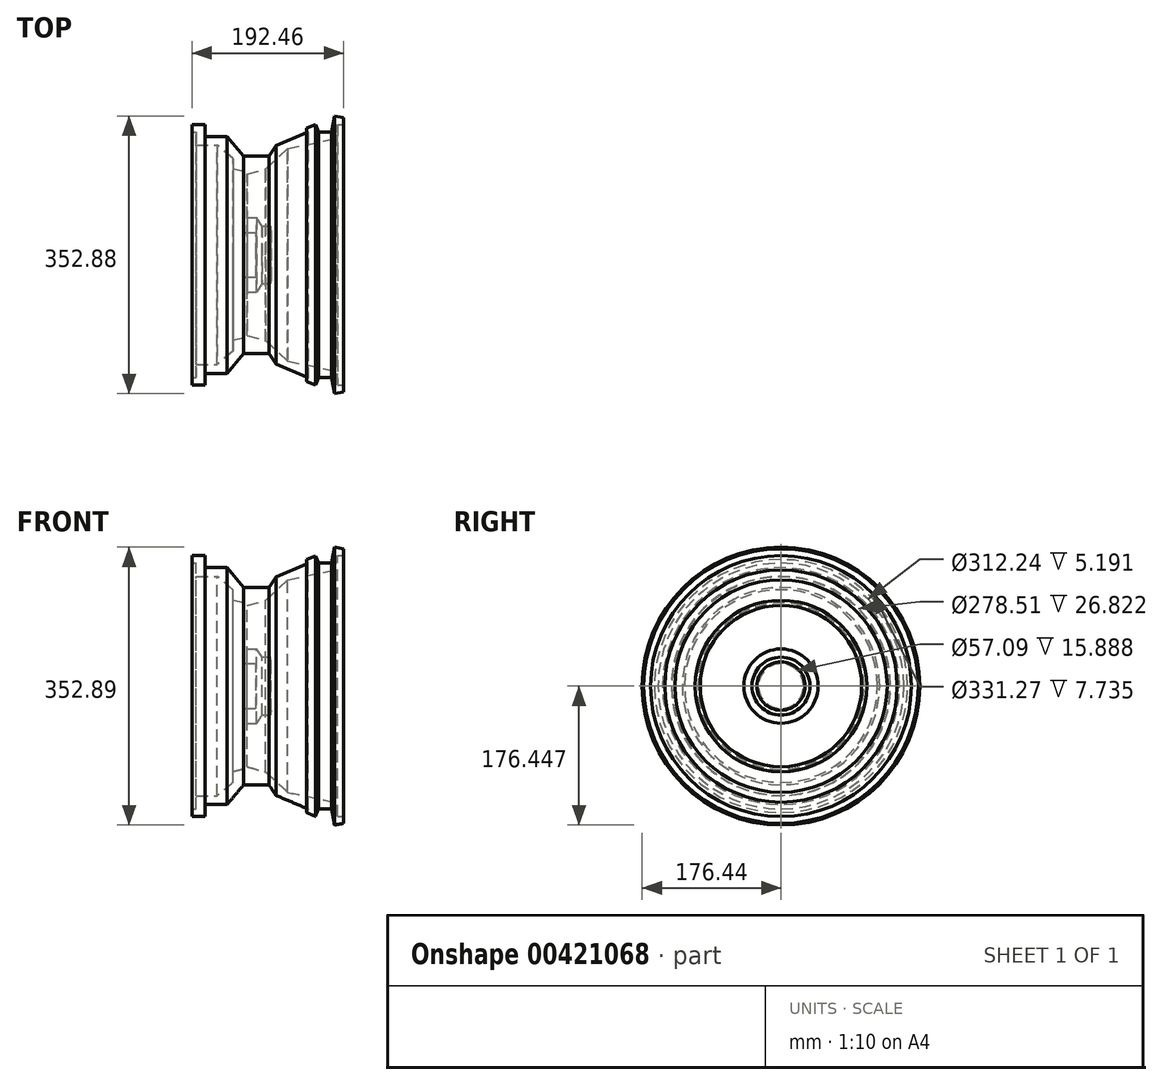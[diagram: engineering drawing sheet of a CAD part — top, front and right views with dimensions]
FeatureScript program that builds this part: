
annotation { "Feature Type Name" : "Feature", "Feature Type Description" : "" }
export const myFeature = defineFeature(function(context is Context, id is Id, definition is map)
    precondition{}
    {
        {
            var Q0;
            Q0=qCreatedBy(makeId("Front.planeOp"),FACE);
            var sketch = newSketch(context, id + "F0", { "sketchPlane" : qUnion([Q0])});
            skLineSegment(sketch, "E0", {"start": v(-30.6, 50.28) * mm, "end": v(-5.54, 50.28) * mm});
            skLineSegment(sketch, "E1", {"start": v(-5.54, 50.28) * mm, "end": v(-5.54, 46.5) * mm});
            skLineSegment(sketch, "E2", {"start": v(-5.54, 46.5) * mm, "end": v(9.91, 49.4) * mm});
            skLineSegment(sketch, "E3", {"start": v(9.91, 49.4) * mm, "end": v(36.73, 45.32) * mm});
            skLineSegment(sketch, "E4", {"start": v(36.73, 45.32) * mm, "end": v(36.73, 29.88) * mm});
            skLineSegment(sketch, "E5", {"start": v(36.73, 29.88) * mm, "end": v(22.15, 11.22) * mm});
            skLineSegment(sketch, "E6", {"start": v(22.15, 11.22) * mm, "end": v(18.07, -13.55) * mm});
            skLineSegment(sketch, "E7", {"start": v(18.07, -13.55) * mm, "end": v(31.19, -23.46) * mm});
            skLineSegment(sketch, "E8", {"start": v(31.19, -23.46) * mm, "end": v(11.37, -29.88) * mm});
            skLineSegment(sketch, "E9", {"start": v(11.37, -29.88) * mm, "end": v(2.33, -12.1) * mm});
            skLineSegment(sketch, "E10", {"start": v(2.33, -12.1) * mm, "end": v(-20.99, -20.26) * mm});
            skLineSegment(sketch, "E11", {"start": v(-20.99, -20.26) * mm, "end": v(-29.44, -6.85) * mm});
            skLineSegment(sketch, "E12", {"start": v(-29.44, -6.85) * mm, "end": v(-29.44, 11.51) * mm});
            skLineSegment(sketch, "E13", {"start": v(-29.44, 11.51) * mm, "end": v(-37.6, 25.21) * mm});
            skLineSegment(sketch, "E14", {"start": v(-37.6, 25.21) * mm, "end": v(-37.6, 39.79) * mm});
            skLineSegment(sketch, "E15", {"start": v(-37.6, 39.79) * mm, "end": v(-62.38, 46.5) * mm});
            skLineSegment(sketch, "E16", {"start": v(-62.38, 46.5) * mm, "end": v(-62.38, 55.23) * mm});
            skLineSegment(sketch, "E17", {"start": v(-62.38, 55.23) * mm, "end": v(-67.33, 55.23) * mm});
            skLineSegment(sketch, "E18", {"start": v(-67.33, 55.23) * mm, "end": v(-67.33, 61.36) * mm});
            skLineSegment(sketch, "E19", {"start": v(-67.33, 61.36) * mm, "end": v(-56.25, 63.69) * mm});
            skLineSegment(sketch, "E20", {"start": v(-56.25, 63.69) * mm, "end": v(-54.07, 53.29) * mm});
            skLineSegment(sketch, "E21", {"start": v(-54.07, 53.29) * mm, "end": v(-46.04, 54.98) * mm});
            skLineSegment(sketch, "E22", {"start": v(-46.04, 54.98) * mm, "end": v(-30.6, 50.28) * mm});
            skSolve(sketch);
        }
        {
            var Q0;
            Q0 = qSketchRegion(id + "F0", true);
            var Q1;
            Q1=sQuery(id+"F0.wireOp",EDGE,"E8");
            revolve(context, id + "F1", {"entities" : qUnion([Q0]), "axis" : qUnion([Q1]), "revolveType" : RevolveType.FULL});
        }
        {
            var Q0;
            Q0=makeQuery(id+"F1.opRevolve","SWEPT_BODY",BODY,{"disambiguationData":[OSD([sQuery(id+"F0.wireOp",EDGE,"E0"),sQuery(id+"F0.wireOp",EDGE,"E1"),sQuery(id+"F0.wireOp",EDGE,"E2"),sQuery(id+"F0.wireOp",EDGE,"E3"),sQuery(id+"F0.wireOp",EDGE,"E4"),sQuery(id+"F0.wireOp",EDGE,"E5"),sQuery(id+"F0.wireOp",EDGE,"E6"),sQuery(id+"F0.wireOp",EDGE,"E7"),sQuery(id+"F0.wireOp",EDGE,"E8"),sQuery(id+"F0.wireOp",EDGE,"E9"),sQuery(id+"F0.wireOp",EDGE,"E10"),sQuery(id+"F0.wireOp",EDGE,"E11"),sQuery(id+"F0.wireOp",EDGE,"E12"),sQuery(id+"F0.wireOp",EDGE,"E13"),sQuery(id+"F0.wireOp",EDGE,"E14"),sQuery(id+"F0.wireOp",EDGE,"E15"),sQuery(id+"F0.wireOp",EDGE,"E16"),sQuery(id+"F0.wireOp",EDGE,"E17"),sQuery(id+"F0.wireOp",EDGE,"E18"),sQuery(id+"F0.wireOp",EDGE,"E19"),sQuery(id+"F0.wireOp",EDGE,"E20"),sQuery(id+"F0.wireOp",EDGE,"E21"),sQuery(id+"F0.wireOp",EDGE,"E22")])]});
            deleteBodies(context, id + "F2", {"entities" : qUnion([Q0])});
        }
        {
            var Q0;
            Q0=qCreatedBy(makeId("Front.planeOp"),FACE);
            var sketch = newSketch(context, id + "F3", { "sketchPlane" : qUnion([Q0])});
            skLineSegment(sketch, "E23", {"start": v(-65.44, 49.85) * mm, "end": v(-49, 49.85) * mm});
            skLineSegment(sketch, "E24", {"start": v(-49, 49.85) * mm, "end": v(-49, 34.71) * mm});
            skLineSegment(sketch, "E25", {"start": v(-49, 34.71) * mm, "end": v(-20.88, 34.71) * mm});
            skLineSegment(sketch, "E26", {"start": v(-20.88, 34.71) * mm, "end": v(0, 9.63) * mm});
            skLineSegment(sketch, "E27", {"start": v(0, 9.63) * mm, "end": v(32.33, 9.63) * mm});
            skLineSegment(sketch, "E28", {"start": v(32.33, 9.63) * mm, "end": v(40.98, 23.04) * mm});
            skLineSegment(sketch, "E29", {"start": v(40.98, 23.04) * mm, "end": v(82.08, 40.34) * mm});
            skLineSegment(sketch, "E30", {"start": v(82.08, 40.34) * mm, "end": v(80.13, 44.96) * mm});
            skLineSegment(sketch, "E31", {"start": v(80.13, 44.96) * mm, "end": v(91.3, 49.66) * mm});
            skLineSegment(sketch, "E32", {"start": v(91.3, 49.66) * mm, "end": v(95.23, 40.34) * mm});
            skLineSegment(sketch, "E33", {"start": v(95.23, 40.34) * mm, "end": v(111.93, 40.34) * mm});
            skLineSegment(sketch, "E34", {"start": v(111.93, 40.34) * mm, "end": v(115.39, 60.66) * mm});
            skLineSegment(sketch, "E35", {"start": v(115.39, 60.66) * mm, "end": v(127.02, 58.68) * mm});
            skLineSegment(sketch, "E36", {"start": v(127.02, 58.68) * mm, "end": v(127.02, 49.85) * mm});
            skLineSegment(sketch, "E37", {"start": v(127.02, 49.85) * mm, "end": v(119.28, 49.85) * mm});
            skLineSegment(sketch, "E38", {"start": v(119.28, 49.85) * mm, "end": v(115.39, 31.69) * mm});
            skLineSegment(sketch, "E39", {"start": v(115.39, 31.69) * mm, "end": v(56.12, 19.15) * mm});
            skLineSegment(sketch, "E40", {"start": v(56.12, 19.15) * mm, "end": v(28, -6.8) * mm});
            skLineSegment(sketch, "E41", {"start": v(28, -6.8) * mm, "end": v(4.64, -13.29) * mm});
            skLineSegment(sketch, "E42", {"start": v(4.64, -13.29) * mm, "end": v(4.64, -68.64) * mm});
            skLineSegment(sketch, "E43", {"start": v(4.64, -68.64) * mm, "end": v(16.75, -68.64) * mm});
            skLineSegment(sketch, "E44", {"start": v(16.75, -68.64) * mm, "end": v(23.24, -79.02) * mm});
            skLineSegment(sketch, "E45", {"start": v(23.24, -79.02) * mm, "end": v(34.06, -79.02) * mm});
            skLineSegment(sketch, "E46", {"start": v(34.06, -79.02) * mm, "end": v(34.92, -85.08) * mm});
            skLineSegment(sketch, "E47", {"start": v(34.92, -85.08) * mm, "end": v(34.92, -115.78) * mm});
            skLineSegment(sketch, "E48", {"start": v(34.92, -115.78) * mm, "end": v(15.89, -115.78) * mm});
            skLineSegment(sketch, "E49", {"start": v(15.89, -115.78) * mm, "end": v(15.89, -87.24) * mm});
            skLineSegment(sketch, "E50", {"start": v(15.89, -87.24) * mm, "end": v(0, -87.24) * mm});
            skLineSegment(sketch, "E51", {"start": v(0, -87.24) * mm, "end": v(0, -10.26) * mm});
            skLineSegment(sketch, "E52", {"start": v(0, -10.26) * mm, "end": v(-13.53, -6.8) * mm});
            skLineSegment(sketch, "E53", {"start": v(-13.53, -6.8) * mm, "end": v(-13.53, 6.6) * mm});
            skLineSegment(sketch, "E54", {"start": v(-13.53, 6.6) * mm, "end": v(-33.43, 23.47) * mm});
            skLineSegment(sketch, "E55", {"start": v(-33.43, 23.47) * mm, "end": v(-60.25, 23.47) * mm});
            skLineSegment(sketch, "E56", {"start": v(-60.25, 23.47) * mm, "end": v(-60.25, 40.34) * mm});
            skLineSegment(sketch, "E57", {"start": v(-60.25, 40.34) * mm, "end": v(-65.44, 40.34) * mm});
            skLineSegment(sketch, "E58", {"start": v(-65.44, 40.34) * mm, "end": v(-65.44, 49.85) * mm});
            skSolve(sketch);
        }
        {
            var Q0;
            Q0=makeQuery(id+"F3.imprint","IMPRINT",FACE,{"disambiguationData":[TD([[makeQuery(id+"F3.imprint","IMPRINT",EDGE,{"derivedFrom":sQuery(id+"F3.wireOp",EDGE,"E23")}),-1.0]])]});
            var Q1;
            Q1=sQuery(id+"F3.wireOp",EDGE,"E48");
            revolve(context, id + "F4", {"entities" : qUnion([Q0]), "axis" : qUnion([Q1]), "revolveType" : RevolveType.FULL});
        }
    });
